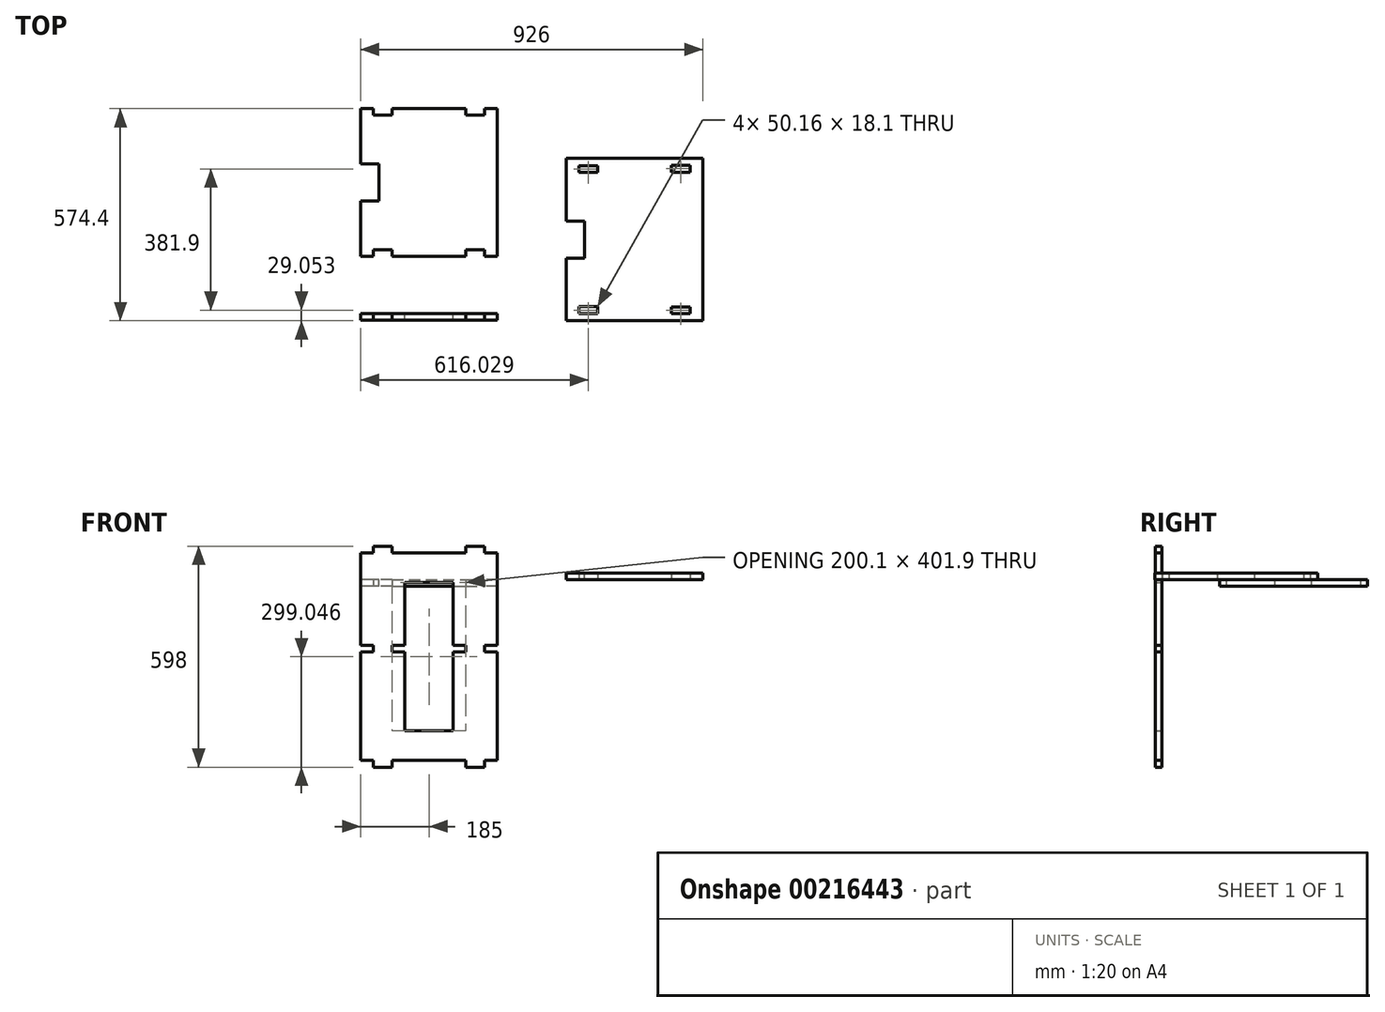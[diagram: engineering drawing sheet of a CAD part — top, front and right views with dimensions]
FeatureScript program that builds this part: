
annotation { "Feature Type Name" : "Feature", "Feature Type Description" : "" }
export const myFeature = defineFeature(function(context is Context, id is Id, definition is map)
    precondition{}
    {
        {
            var Q0;
            Q0=qCreatedBy(makeId("Front.planeOp"),FACE);
            var sketch = newSketch(context, id + "F0", { "sketchPlane" : qUnion([Q0])});
            skLineSegment(sketch, "E0.top", {"start": v(-150, -489.22) * mm, "end": v(-100, -489.22) * mm});
            skLineSegment(sketch, "E0.left", {"start": v(-185, 90.78) * mm, "end": v(-185, -159.22) * mm});
            skLineSegment(sketch, "E0.right", {"start": v(-65, 110.78) * mm, "end": v(-65, 108.78) * mm});
            skLineSegment(sketch, "E1.bottom", {"start": v(0, 0) * mm, "end": v(0, 0) * mm});
            skLineSegment(sketch, "E1.top", {"start": v(0, 122.84) * mm, "end": v(0, 122.84) * mm});
            skLineSegment(sketch, "E1.left", {"start": v(0, 0) * mm, "end": v(0, 10.78) * mm, "construction": true});
            skLineSegment(sketch, "E1.right", {"start": v(0, 0) * mm, "end": v(0, 10.78) * mm, "construction": true});
            skPoint(sketch, "E2.visualSharp", {"position": v(-185, 108.78) * mm});
            skPoint(sketch, "E3", {"position": v(-185, -159.22) * mm});
            skPoint(sketch, "E4", {"position": v(-185, 92.78) * mm});
            skPoint(sketch, "E5", {"position": v(-185, -177.32) * mm});
            skLineSegment(sketch, "E6.bottom", {"start": v(-185, -159.22) * mm, "end": v(-150, -159.22) * mm});
            skLineSegment(sketch, "E6.top", {"start": v(-185, -177.32) * mm, "end": v(-150, -177.32) * mm});
            skPoint(sketch, "E7", {"position": v(-185, -471.12) * mm});
            skLineSegment(sketch, "E8.top", {"start": v(-150, -489.22) * mm, "end": v(-125, -489.22) * mm});
            skLineSegment(sketch, "E9", {"start": v(-185, 90.78) * mm, "end": v(-150, 90.78) * mm});
            skLineSegment(sketch, "E10", {"start": v(-150, 90.78) * mm, "end": v(-150, 108.78) * mm});
            skPoint(sketch, "E11", {"position": v(-125, 108.78) * mm});
            skLineSegment(sketch, "E12", {"start": v(-125, 108.78) * mm, "end": v(-125, 56.52) * mm, "construction": true});
            skLineSegment(sketch, "E13.bottom", {"start": v(-185, -471.12) * mm, "end": v(-150, -471.12) * mm});
            skLineSegment(sketch, "E13.right", {"start": v(-150, -471.12) * mm, "end": v(-150, -489.22) * mm});
            skLineSegment(sketch, "E14.MirrorCS", {"start": v(-65, -159.22) * mm, "end": v(-100, -159.22) * mm});
            skLineSegment(sketch, "E15.MirrorCS", {"start": v(-65, -177.32) * mm, "end": v(-100, -177.32) * mm});
            skLineSegment(sketch, "E16.MirrorCS", {"start": v(-65, -471.12) * mm, "end": v(-100, -471.12) * mm});
            skLineSegment(sketch, "E17.MirrorCS", {"start": v(-100, -471.12) * mm, "end": v(-100, -489.22) * mm});
            skPoint(sketch, "E18.orphan", {"position": v(-65, -489.22) * mm});
            skPoint(sketch, "E19.MirrorCS.end.orphan", {"position": v(-100, -489.22) * mm});
            skPoint(sketch, "E13.top.start.orphan", {"position": v(-185, -489.22) * mm});
            skLineSegment(sketch, "E20.trimOffspring", {"start": v(-185, -177.32) * mm, "end": v(-185, -471.12) * mm});
            skLineSegment(sketch, "E21.trimOffspring", {"start": v(-65, -177.32) * mm, "end": v(-65, -391.12) * mm});
            skPoint(sketch, "E22", {"position": v(-99.94, 108.78) * mm});
            skLineSegment(sketch, "E23.top", {"start": v(-99.94, 90.78) * mm, "end": v(-65, 90.78) * mm});
            skLineSegment(sketch, "E23.left", {"start": v(-99.94, 108.78) * mm, "end": v(-99.94, 90.78) * mm});
            skLineSegment(sketch, "E24.trimOffspring", {"start": v(-65, 10.78) * mm, "end": v(-65, -159.22) * mm});
            skLineSegment(sketch, "E25", {"start": v(-99.94, 108.78) * mm, "end": v(-150, 108.78) * mm});
            skLineSegment(sketch, "E26", {"start": v(-65, 90.78) * mm, "end": v(0, 90.78) * mm});
            skLineSegment(sketch, "E27", {"start": v(-65, 10.78) * mm, "end": v(0, 10.78) * mm});
            skLineSegment(sketch, "E28.trimOffspring", {"start": v(0, 90.78) * mm, "end": v(0, 122.84) * mm, "construction": true});
            skLineSegment(sketch, "E29", {"start": v(-65, -471.12) * mm, "end": v(0, -471.12) * mm});
            skLineSegment(sketch, "E30.0", {"start": v(-65, -391.12) * mm, "end": v(0, -391.12) * mm});
            skLineSegment(sketch, "E31.MirrorCS", {"start": v(65, 90.78) * mm, "end": v(0, 90.78) * mm});
            skLineSegment(sketch, "E32.MirrorCS", {"start": v(65, 10.78) * mm, "end": v(0, 10.78) * mm});
            skLineSegment(sketch, "E33.MirrorCS", {"start": v(99.94, 90.78) * mm, "end": v(65, 90.78) * mm});
            skLineSegment(sketch, "E34.MirrorCS", {"start": v(99.94, 108.78) * mm, "end": v(99.94, 90.78) * mm});
            skLineSegment(sketch, "E35.MirrorCS", {"start": v(99.94, 108.78) * mm, "end": v(150, 108.78) * mm});
            skLineSegment(sketch, "E36.MirrorCS", {"start": v(150, 90.78) * mm, "end": v(150, 108.78) * mm});
            skLineSegment(sketch, "E37.MirrorCS", {"start": v(185, 90.78) * mm, "end": v(150, 90.78) * mm});
            skLineSegment(sketch, "E38.MirrorCS", {"start": v(185, 90.78) * mm, "end": v(185, -159.22) * mm});
            skLineSegment(sketch, "E39.MirrorCS", {"start": v(65, 10.78) * mm, "end": v(65, -159.22) * mm});
            skLineSegment(sketch, "E40.MirrorCS", {"start": v(65, -159.22) * mm, "end": v(100, -159.22) * mm});
            skLineSegment(sketch, "E41.MirrorCS", {"start": v(65, -177.32) * mm, "end": v(100, -177.32) * mm});
            skLineSegment(sketch, "E42.MirrorCS", {"start": v(185, -177.32) * mm, "end": v(150, -177.32) * mm});
            skLineSegment(sketch, "E43.MirrorCS", {"start": v(185, -159.22) * mm, "end": v(150, -159.22) * mm});
            skLineSegment(sketch, "E44.MirrorCS", {"start": v(185, -177.32) * mm, "end": v(185, -471.12) * mm});
            skLineSegment(sketch, "E45.MirrorCS", {"start": v(65, -177.32) * mm, "end": v(65, -391.12) * mm});
            skLineSegment(sketch, "E46.MirrorCS", {"start": v(65, -471.12) * mm, "end": v(100, -471.12) * mm});
            skLineSegment(sketch, "E47.MirrorCS", {"start": v(185, -471.12) * mm, "end": v(150, -471.12) * mm});
            skLineSegment(sketch, "E48.MirrorCS", {"start": v(150, -489.22) * mm, "end": v(125, -489.22) * mm});
            skLineSegment(sketch, "E49.MirrorCS", {"start": v(150, -489.22) * mm, "end": v(100, -489.22) * mm});
            skLineSegment(sketch, "E50.MirrorCS", {"start": v(100, -471.12) * mm, "end": v(100, -489.22) * mm});
            skLineSegment(sketch, "E51.MirrorCS", {"start": v(150, -471.12) * mm, "end": v(150, -489.22) * mm});
            skLineSegment(sketch, "E52.MirrorCS", {"start": v(65, -391.12) * mm, "end": v(0, -391.12) * mm});
            skLineSegment(sketch, "E53.MirrorCS", {"start": v(65, -471.12) * mm, "end": v(0, -471.12) * mm});
            skPoint(sketch, "E54.orphan", {"position": v(65, -471.12) * mm});
            skPoint(sketch, "E55.orphan", {"position": v(65, 90.78) * mm});
            skLineSegment(sketch, "E56.0", {"start": v(-149.95, -159.22) * mm, "end": v(-149.95, -177.32) * mm});
            skLineSegment(sketch, "E57", {"start": v(-149.95, -159.22) * mm, "end": v(-150, -159.22) * mm});
            skLineSegment(sketch, "E58", {"start": v(-150, -177.32) * mm, "end": v(-149.95, -177.32) * mm});
            skLineSegment(sketch, "E59.0", {"start": v(-100.05, -159.22) * mm, "end": v(-100.05, -177.32) * mm});
            skPoint(sketch, "E60.MirrorCS.end.orphan", {"position": v(-100, -177.32) * mm});
            skPoint(sketch, "E60.MirrorCS.start.orphan", {"position": v(-100, -159.22) * mm});
            skLineSegment(sketch, "E61", {"start": v(-100.05, -159.22) * mm, "end": v(-100, -159.22) * mm});
            skLineSegment(sketch, "E62", {"start": v(-100, -177.32) * mm, "end": v(-100.05, -177.32) * mm});
            skLineSegment(sketch, "E63.0", {"start": v(100.05, -159.22) * mm, "end": v(100.05, -177.32) * mm});
            skLineSegment(sketch, "E64.0", {"start": v(149.95, -159.22) * mm, "end": v(149.95, -177.32) * mm});
            skPoint(sketch, "E65.MirrorCS.end.orphan", {"position": v(100, -177.32) * mm});
            skPoint(sketch, "E65.MirrorCS.start.orphan", {"position": v(100, -159.22) * mm});
            skLineSegment(sketch, "E66", {"start": v(100.05, -159.22) * mm, "end": v(100, -159.22) * mm});
            skLineSegment(sketch, "E67", {"start": v(100, -177.32) * mm, "end": v(100.05, -177.32) * mm});
            skPoint(sketch, "E68.MirrorCS.end.orphan", {"position": v(150, -177.32) * mm});
            skPoint(sketch, "E68.MirrorCS.start.orphan", {"position": v(150, -159.22) * mm});
            skLineSegment(sketch, "E69", {"start": v(150, -177.32) * mm, "end": v(149.95, -177.32) * mm});
            skLineSegment(sketch, "E70", {"start": v(150, -159.22) * mm, "end": v(149.95, -159.22) * mm});
            skSolve(sketch);
        }
        {
            var Q0;
            Q0=qCreatedBy(makeId("Top.planeOp"),FACE);
            var sketch = newSketch(context, id + "F1", { "sketchPlane" : qUnion([Q0])});
            skPoint(sketch, "E71.0", {"position": v(-185, 0) * mm});
            skPoint(sketch, "E72.0", {"position": v(-150, 0) * mm});
            skPoint(sketch, "E73.0", {"position": v(-99.94, 0) * mm});
            skPoint(sketch, "E74.0", {"position": v(99.94, 0) * mm});
            skPoint(sketch, "E75.0", {"position": v(185, 0) * mm});
            skPoint(sketch, "E76.0", {"position": v(150, 0) * mm});
            skLineSegment(sketch, "E77", {"start": v(-150, 0) * mm, "end": v(-150, 18) * mm});
            skLineSegment(sketch, "E78", {"start": v(-99.94, 0) * mm, "end": v(-99.94, 18) * mm});
            skLineSegment(sketch, "E79", {"start": v(-99.94, 18) * mm, "end": v(-150, 18) * mm});
            skLineSegment(sketch, "E80", {"start": v(-99.94, 0) * mm, "end": v(99.94, 0) * mm});
            skLineSegment(sketch, "E81", {"start": v(99.94, 18) * mm, "end": v(150, 18) * mm});
            skLineSegment(sketch, "E82", {"start": v(99.94, 18) * mm, "end": v(99.94, 0) * mm});
            skLineSegment(sketch, "E83", {"start": v(150, 18) * mm, "end": v(150, 0) * mm});
            skLineSegment(sketch, "E84", {"start": v(185, 0) * mm, "end": v(150, 0) * mm});
            skLineSegment(sketch, "E85", {"start": v(-150, 0) * mm, "end": v(-185, 0) * mm});
            skPoint(sketch, "E86.end.orphan", {"position": v(-185, 18) * mm});
            skLineSegment(sketch, "E87", {"start": v(185, 0) * mm, "end": v(185, 200) * mm});
            skLineSegment(sketch, "E88", {"start": v(185, 200) * mm, "end": v(114.01, 200) * mm, "construction": true});
            skLineSegment(sketch, "E89", {"start": v(-185, 0) * mm, "end": v(-185, 200) * mm});
            skLineSegment(sketch, "E90.MirrorCS", {"start": v(185, 400) * mm, "end": v(185, 200) * mm});
            skLineSegment(sketch, "E91.MirrorCS", {"start": v(99.94, 382) * mm, "end": v(150, 382) * mm});
            skLineSegment(sketch, "E92.MirrorCS", {"start": v(185, 400) * mm, "end": v(150, 400) * mm});
            skLineSegment(sketch, "E93.MirrorCS", {"start": v(150, 382) * mm, "end": v(150, 400) * mm});
            skLineSegment(sketch, "E94.MirrorCS", {"start": v(99.94, 382) * mm, "end": v(99.94, 400) * mm});
            skLineSegment(sketch, "E95.MirrorCS", {"start": v(-99.94, 400) * mm, "end": v(99.94, 400) * mm});
            skLineSegment(sketch, "E96.MirrorCS", {"start": v(-99.94, 400) * mm, "end": v(-99.94, 382) * mm});
            skLineSegment(sketch, "E97.MirrorCS", {"start": v(-99.94, 382) * mm, "end": v(-150, 382) * mm});
            skLineSegment(sketch, "E98.MirrorCS", {"start": v(-150, 400) * mm, "end": v(-150, 382) * mm});
            skLineSegment(sketch, "E99.MirrorCS", {"start": v(-150, 400) * mm, "end": v(-185, 400) * mm});
            skLineSegment(sketch, "E100.MirrorCS", {"start": v(-185, 400) * mm, "end": v(-185, 200) * mm});
            skSolve(sketch);
        }
        {
            var Q0;
            Q0=makeQuery(id+"F1.imprint","IMPRINT",FACE,{"disambiguationData":[TD([[makeQuery(id+"F1.imprint","IMPRINT",EDGE,{"derivedFrom":sQuery(id+"F1.wireOp",EDGE,"E77")}),1.0]])]});
            extrude(context, id + "F2", {"entities" : qUnion([Q0]), "depth" : 18 * mm});
        }
        {
            var Q0;
            Q0=makeQuery(id+"F0.imprint","IMPRINT",FACE,{"disambiguationData":[TD([[makeQuery(id+"F0.imprint","IMPRINT",EDGE,{"derivedFrom":sQuery(id+"F0.wireOp",EDGE,"E0.top")}),1.0]])]});
            extrude(context, id + "F3", {"entities" : qUnion([Q0]), "depth" : 18 * mm});
        }
        {
            var Q0;
            Q0=makeQuery(id+"F2.opExtrude","SWEPT_BODY",BODY,{"disambiguationData":[OSD([sQuery(id+"F1.wireOp",EDGE,"E77"),sQuery(id+"F1.wireOp",EDGE,"E78"),sQuery(id+"F1.wireOp",EDGE,"E79"),sQuery(id+"F1.wireOp",EDGE,"E80"),sQuery(id+"F1.wireOp",EDGE,"E81"),sQuery(id+"F1.wireOp",EDGE,"E82"),sQuery(id+"F1.wireOp",EDGE,"E83"),sQuery(id+"F1.wireOp",EDGE,"E84"),sQuery(id+"F1.wireOp",EDGE,"E85"),sQuery(id+"F1.wireOp",EDGE,"E87"),sQuery(id+"F1.wireOp",EDGE,"E89"),sQuery(id+"F1.wireOp",EDGE,"E90.MirrorCS"),sQuery(id+"F1.wireOp",EDGE,"E91.MirrorCS"),sQuery(id+"F1.wireOp",EDGE,"E92.MirrorCS"),sQuery(id+"F1.wireOp",EDGE,"E93.MirrorCS"),sQuery(id+"F1.wireOp",EDGE,"E94.MirrorCS"),sQuery(id+"F1.wireOp",EDGE,"E95.MirrorCS"),sQuery(id+"F1.wireOp",EDGE,"E96.MirrorCS"),sQuery(id+"F1.wireOp",EDGE,"E97.MirrorCS"),sQuery(id+"F1.wireOp",EDGE,"E98.MirrorCS"),sQuery(id+"F1.wireOp",EDGE,"E99.MirrorCS"),sQuery(id+"F1.wireOp",EDGE,"E100.MirrorCS")])]});
            transform(context, id + "F4", {"entities" : qUnion([Q0]), "transformType" : TransformType.TRANSLATION_3D, "dx" : 0 * mm, "dy" : 155 * mm, "dz" : 0 * mm, "makeCopy" : false});
        }
        {
            var Q0;
            Q0=makeQuery(id+"F2.opExtrude","CAP_FACE",FACE,{"disambiguationData":[OSD([sQuery(id+"F1.wireOp",EDGE,"E77"),sQuery(id+"F1.wireOp",EDGE,"E78"),sQuery(id+"F1.wireOp",EDGE,"E79"),sQuery(id+"F1.wireOp",EDGE,"E80"),sQuery(id+"F1.wireOp",EDGE,"E81"),sQuery(id+"F1.wireOp",EDGE,"E82"),sQuery(id+"F1.wireOp",EDGE,"E83"),sQuery(id+"F1.wireOp",EDGE,"E84"),sQuery(id+"F1.wireOp",EDGE,"E85"),sQuery(id+"F1.wireOp",EDGE,"E87"),sQuery(id+"F1.wireOp",EDGE,"E89"),sQuery(id+"F1.wireOp",EDGE,"E90.MirrorCS"),sQuery(id+"F1.wireOp",EDGE,"E91.MirrorCS"),sQuery(id+"F1.wireOp",EDGE,"E92.MirrorCS"),sQuery(id+"F1.wireOp",EDGE,"E93.MirrorCS"),sQuery(id+"F1.wireOp",EDGE,"E94.MirrorCS"),sQuery(id+"F1.wireOp",EDGE,"E95.MirrorCS"),sQuery(id+"F1.wireOp",EDGE,"E96.MirrorCS"),sQuery(id+"F1.wireOp",EDGE,"E97.MirrorCS"),sQuery(id+"F1.wireOp",EDGE,"E98.MirrorCS"),sQuery(id+"F1.wireOp",EDGE,"E99.MirrorCS"),sQuery(id+"F1.wireOp",EDGE,"E100.MirrorCS")])],"isStart":false});
            var sketch = newSketch(context, id + "F5", { "sketchPlane" : qUnion([Q0])});
            skLineSegment(sketch, "E101.0", {"start": v(-150.05, 400.6) * mm, "end": v(-99.9, 400.6) * mm});
            skLineSegment(sketch, "E101.1", {"start": v(-150.05, 400.6) * mm, "end": v(-150.05, 382.5) * mm});
            skLineSegment(sketch, "E101.2", {"start": v(-99.9, 382.5) * mm, "end": v(-150.05, 382.5) * mm});
            skLineSegment(sketch, "E101.3", {"start": v(-99.9, 400.6) * mm, "end": v(-99.9, 382.5) * mm});
            skPoint(sketch, "E102.0.end.orphan", {"position": v(-99.94, 537) * mm});
            skPoint(sketch, "E103.0.end.orphan", {"position": v(-150, 537) * mm});
            skPoint(sketch, "E104.end.orphan", {"position": v(-99.94, 555) * mm});
            skPoint(sketch, "E104.start.orphan", {"position": v(-150, 555) * mm});
            skLineSegment(sketch, "E105.0", {"start": v(99.9, 401.16) * mm, "end": v(150.05, 401.16) * mm});
            skLineSegment(sketch, "E105.1", {"start": v(99.9, 383.06) * mm, "end": v(99.9, 401.16) * mm});
            skLineSegment(sketch, "E105.2", {"start": v(99.9, 383.06) * mm, "end": v(150.05, 383.06) * mm});
            skLineSegment(sketch, "E105.3", {"start": v(150.05, 383.06) * mm, "end": v(150.05, 401.16) * mm});
            skPoint(sketch, "E106.start.orphan", {"position": v(99.94, 555) * mm});
            skPoint(sketch, "E107.0.end.orphan", {"position": v(150, 555) * mm});
            skPoint(sketch, "E108.0.end.orphan", {"position": v(150, 537) * mm});
            skPoint(sketch, "E108.0.start.orphan", {"position": v(99.94, 537) * mm});
            skPoint(sketch, "E109", {"position": v(-102.1, 182.5) * mm});
            skLineSegment(sketch, "E110", {"start": v(-102.1, 182.5) * mm, "end": v(-32.8, 182.5) * mm, "construction": true});
            skPoint(sketch, "E111.0.end.orphan", {"position": v(-185, 155) * mm});
            skPoint(sketch, "E111.0.start.orphan", {"position": v(-185, 555) * mm});
            skLineSegment(sketch, "E112.0.0", {"start": v(185, 155) * mm, "end": v(185, 420.6) * mm});
            skLineSegment(sketch, "E112.0.2", {"start": v(185, 420.6) * mm, "end": v(185, 155) * mm});
            skLineSegment(sketch, "E113", {"start": v(-185, 420.6) * mm, "end": v(185, 420.6) * mm});
            skPoint(sketch, "E114.orphan", {"position": v(185, 555) * mm});
            skPoint(sketch, "E115", {"position": v(-185, 200.6) * mm});
            skLineSegment(sketch, "E116", {"start": v(-185, 420.6) * mm, "end": v(-185, 200.6) * mm});
            skLineSegment(sketch, "E117", {"start": v(185, 420.6) * mm, "end": v(185, 200.6) * mm});
            skLineSegment(sketch, "E118", {"start": v(185, 200.6) * mm, "end": v(90.23, 200.6) * mm, "construction": true});
            skLineSegment(sketch, "E119.MirrorCS", {"start": v(-99.9, 18.7) * mm, "end": v(-150.05, 18.7) * mm});
            skLineSegment(sketch, "E120.MirrorCS", {"start": v(-150.05, 0.6) * mm, "end": v(-150.05, 18.7) * mm});
            skLineSegment(sketch, "E121.MirrorCS", {"start": v(-150.05, 0.6) * mm, "end": v(-99.9, 0.6) * mm});
            skLineSegment(sketch, "E122.MirrorCS", {"start": v(-99.9, 0.6) * mm, "end": v(-99.9, 18.7) * mm});
            skLineSegment(sketch, "E123.MirrorCS", {"start": v(99.9, 18.15) * mm, "end": v(99.9, 0.05) * mm});
            skLineSegment(sketch, "E124.MirrorCS", {"start": v(99.9, 18.15) * mm, "end": v(150.05, 18.15) * mm});
            skLineSegment(sketch, "E125.MirrorCS", {"start": v(150.05, 18.15) * mm, "end": v(150.05, 0.05) * mm});
            skLineSegment(sketch, "E126.MirrorCS", {"start": v(99.9, 0.05) * mm, "end": v(150.05, 0.05) * mm});
            skLineSegment(sketch, "E127.MirrorCS", {"start": v(185, -19.4) * mm, "end": v(185, 246.2) * mm});
            skLineSegment(sketch, "E128.MirrorCS", {"start": v(-185, -19.4) * mm, "end": v(-185, 200.6) * mm});
            skLineSegment(sketch, "E129.MirrorCS", {"start": v(-185, -19.4) * mm, "end": v(185, -19.4) * mm});
            skSolve(sketch);
        }
        {
            var Q0;
            Q0=makeQuery(id+"F5.imprint","IMPRINT",FACE,{"disambiguationData":[TD([[makeQuery(id+"F5.imprint","IMPRINT",EDGE,{"derivedFrom":sQuery(id+"F5.wireOp",EDGE,"E101.0")}),1.0]])]});
            var Q1;
            Q1=makeQuery(id+"F5.imprint","IMPRINT",FACE,{"disambiguationData":[TD([[makeQuery(id+"F5.imprint","IMPRINT",EDGE,{"derivedFrom":sQuery(id+"F5.wireOp",EDGE,"E119.MirrorCS")}),-1.0]])]});
            extrude(context, id + "F6", {"entities" : qUnion([Q0, Q1]), "depth" : 18 * mm});
        }
        {
            var Q0;
            Q0=makeQuery(id+"F6.opExtrude","SWEPT_BODY",BODY,{"disambiguationData":[OSD([sQuery(id+"F5.wireOp",EDGE,"E101.0"),sQuery(id+"F5.wireOp",EDGE,"E101.1"),sQuery(id+"F5.wireOp",EDGE,"E101.2"),sQuery(id+"F5.wireOp",EDGE,"E101.3"),sQuery(id+"F5.wireOp",EDGE,"E105.0"),sQuery(id+"F5.wireOp",EDGE,"E105.1"),sQuery(id+"F5.wireOp",EDGE,"E105.2"),sQuery(id+"F5.wireOp",EDGE,"E105.3"),sQuery(id+"F5.wireOp",EDGE,"E113"),sQuery(id+"F5.wireOp",EDGE,"E116"),sQuery(id+"F5.wireOp",EDGE,"E117"),sQuery(id+"F5.wireOp",EDGE,"E119.MirrorCS"),sQuery(id+"F5.wireOp",EDGE,"E120.MirrorCS"),sQuery(id+"F5.wireOp",EDGE,"E121.MirrorCS"),sQuery(id+"F5.wireOp",EDGE,"E122.MirrorCS"),sQuery(id+"F5.wireOp",EDGE,"E123.MirrorCS"),sQuery(id+"F5.wireOp",EDGE,"E124.MirrorCS"),sQuery(id+"F5.wireOp",EDGE,"E125.MirrorCS"),sQuery(id+"F5.wireOp",EDGE,"E126.MirrorCS"),sQuery(id+"F5.wireOp",EDGE,"E127.MirrorCS"),sQuery(id+"F5.wireOp",EDGE,"E128.MirrorCS"),sQuery(id+"F5.wireOp",EDGE,"E129.MirrorCS")])]});
            transform(context, id + "F7", {"entities" : qUnion([Q0]), "transformType" : TransformType.TRANSLATION_3D, "dx" : 556 * mm, "dy" : 0 * mm, "dz" : 0 * mm, "makeCopy" : false});
        }
        {
            var Q0;
            Q0=makeQuery(id+"F6.opExtrude","CAP_FACE",FACE,{"disambiguationData":[OSD([sQuery(id+"F5.wireOp",EDGE,"E101.0"),sQuery(id+"F5.wireOp",EDGE,"E101.1"),sQuery(id+"F5.wireOp",EDGE,"E101.2"),sQuery(id+"F5.wireOp",EDGE,"E101.3"),sQuery(id+"F5.wireOp",EDGE,"E105.0"),sQuery(id+"F5.wireOp",EDGE,"E105.1"),sQuery(id+"F5.wireOp",EDGE,"E105.2"),sQuery(id+"F5.wireOp",EDGE,"E105.3"),sQuery(id+"F5.wireOp",EDGE,"E113"),sQuery(id+"F5.wireOp",EDGE,"E116"),sQuery(id+"F5.wireOp",EDGE,"E117"),sQuery(id+"F5.wireOp",EDGE,"E119.MirrorCS"),sQuery(id+"F5.wireOp",EDGE,"E120.MirrorCS"),sQuery(id+"F5.wireOp",EDGE,"E121.MirrorCS"),sQuery(id+"F5.wireOp",EDGE,"E122.MirrorCS"),sQuery(id+"F5.wireOp",EDGE,"E123.MirrorCS"),sQuery(id+"F5.wireOp",EDGE,"E124.MirrorCS"),sQuery(id+"F5.wireOp",EDGE,"E125.MirrorCS"),sQuery(id+"F5.wireOp",EDGE,"E126.MirrorCS"),sQuery(id+"F5.wireOp",EDGE,"E127.MirrorCS"),sQuery(id+"F5.wireOp",EDGE,"E128.MirrorCS"),sQuery(id+"F5.wireOp",EDGE,"E129.MirrorCS")])],"isStart":false});
            var sketch = newSketch(context, id + "F8", { "sketchPlane" : qUnion([Q0])});
            skLineSegment(sketch, "E130.0.0", {"start": v(371, 420.6) * mm, "end": v(371, -19.4) * mm});
            skLineSegment(sketch, "E130.0.1", {"start": v(371, -19.4) * mm, "end": v(741, -19.4) * mm});
            skLineSegment(sketch, "E130.0.2", {"start": v(741, -19.4) * mm, "end": v(741, 420.6) * mm});
            skLineSegment(sketch, "E130.0.3", {"start": v(741, 420.6) * mm, "end": v(371, 420.6) * mm});
            skLineSegment(sketch, "E131.0.0", {"start": v(-99.94, 555) * mm, "end": v(-99.94, 537) * mm});
            skLineSegment(sketch, "E131.0.1", {"start": v(-99.94, 537) * mm, "end": v(-150, 537) * mm});
            skLineSegment(sketch, "E131.0.2", {"start": v(-150, 537) * mm, "end": v(-150, 555) * mm});
            skLineSegment(sketch, "E131.0.3", {"start": v(-150, 555) * mm, "end": v(-185, 555) * mm});
            skLineSegment(sketch, "E131.0.4", {"start": v(-185, 555) * mm, "end": v(-185, 155) * mm});
            skLineSegment(sketch, "E131.0.5", {"start": v(-185, 155) * mm, "end": v(-150, 155) * mm});
            skLineSegment(sketch, "E131.0.6", {"start": v(-150, 155) * mm, "end": v(-150, 173) * mm});
            skLineSegment(sketch, "E131.0.7", {"start": v(-150, 173) * mm, "end": v(-99.94, 173) * mm});
            skLineSegment(sketch, "E131.0.8", {"start": v(-99.94, 173) * mm, "end": v(-99.94, 155) * mm});
            skLineSegment(sketch, "E131.0.9", {"start": v(-99.94, 155) * mm, "end": v(99.94, 155) * mm});
            skLineSegment(sketch, "E131.0.10", {"start": v(99.94, 155) * mm, "end": v(99.94, 173) * mm});
            skLineSegment(sketch, "E131.0.11", {"start": v(99.94, 173) * mm, "end": v(150, 173) * mm});
            skLineSegment(sketch, "E131.0.12", {"start": v(150, 173) * mm, "end": v(150, 155) * mm});
            skLineSegment(sketch, "E131.0.13", {"start": v(150, 155) * mm, "end": v(185, 155) * mm});
            skLineSegment(sketch, "E131.0.14", {"start": v(185, 155) * mm, "end": v(185, 555) * mm});
            skLineSegment(sketch, "E131.0.15", {"start": v(185, 555) * mm, "end": v(150, 555) * mm});
            skLineSegment(sketch, "E131.0.16", {"start": v(150, 555) * mm, "end": v(150, 537) * mm});
            skLineSegment(sketch, "E131.0.17", {"start": v(150, 537) * mm, "end": v(99.94, 537) * mm});
            skLineSegment(sketch, "E131.0.18", {"start": v(99.94, 537) * mm, "end": v(99.94, 555) * mm});
            skLineSegment(sketch, "E131.0.19", {"start": v(99.94, 555) * mm, "end": v(-99.94, 555) * mm});
            skPoint(sketch, "E132", {"position": v(-185, 355) * mm});
            skPoint(sketch, "E133", {"position": v(371, 200.6) * mm});
            skLineSegment(sketch, "E134.bottom", {"start": v(-135, 405) * mm, "end": v(-235, 405) * mm});
            skLineSegment(sketch, "E134.top", {"start": v(-135, 305) * mm, "end": v(-235, 305) * mm});
            skLineSegment(sketch, "E134.left", {"start": v(-135, 405) * mm, "end": v(-135, 305) * mm});
            skLineSegment(sketch, "E134.right", {"start": v(-235, 405) * mm, "end": v(-235, 305) * mm});
            skLineSegment(sketch, "E135.bottom", {"start": v(421, 250.6) * mm, "end": v(321, 250.6) * mm});
            skLineSegment(sketch, "E135.top", {"start": v(421, 150.6) * mm, "end": v(321, 150.6) * mm});
            skLineSegment(sketch, "E135.left", {"start": v(421, 250.6) * mm, "end": v(421, 150.6) * mm});
            skLineSegment(sketch, "E135.right", {"start": v(321, 250.6) * mm, "end": v(321, 150.6) * mm});
            skSolve(sketch);
        }
        {
            var Q0;
            {var subQ5=sQuery(id+"F8.wireOp",EDGE,"E134.left");Q0=makeQuery(id+"F8.imprint","IMPRINT",FACE,{"disambiguationData":[TD([[makeQuery(id+"F8.imprint","IMPRINT",EDGE,{"derivedFrom":subQ5}),-1.0]])]});}
            var Q1;
            {var subQ5=sQuery(id+"F8.wireOp",EDGE,"E135.left");Q1=makeQuery(id+"F8.imprint","IMPRINT",FACE,{"disambiguationData":[TD([[makeQuery(id+"F8.imprint","IMPRINT",EDGE,{"derivedFrom":subQ5}),-1.0]])]});}
            extrude(context, id + "F9", {"entities" : qUnion([Q0, Q1]), "operationType" : NewBodyOperationType.REMOVE, "oppositeDirection" : true, "depth" : 45 * mm});
        }
    });
